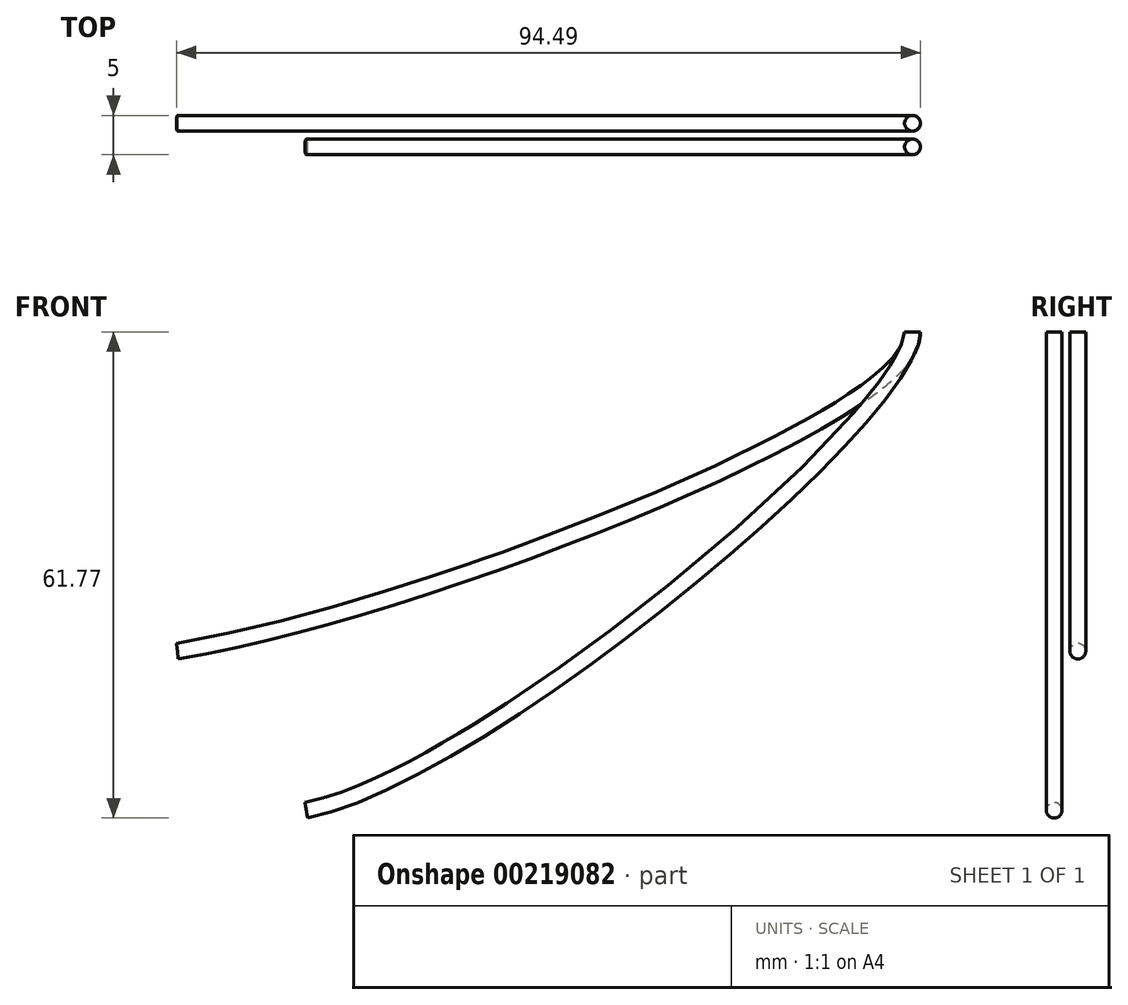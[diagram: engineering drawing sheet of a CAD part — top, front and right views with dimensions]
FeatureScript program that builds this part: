
annotation { "Feature Type Name" : "Feature", "Feature Type Description" : "" }
export const myFeature = defineFeature(function(context is Context, id is Id, definition is map)
    precondition{}
    {
        {
            var Q0;
            Q0=qCreatedBy(makeId("Front.planeOp"),FACE);
            var sketch = newSketch(context, id + "F0", { "sketchPlane" : qUnion([Q0])});
            skLineSegment(sketch, "E0", {"start": v(-1.5, 0) * mm, "end": v(1.5, 0) * mm, "construction": true});
            skFitSpline(sketch, "E1", {"points": [v(-1.5, 0) * mm, v(-93.55, -39.07) * mm], "startDerivative": vector(1.4, -27.44) * mm, "endDerivative": vector(-96.15, -16.1) * mm});
            skFitSpline(sketch, "E2", {"points": [v(1.5, 0) * mm, v(-76.76, -62.26) * mm], "startDerivative": vector(0.49, -35.49) * mm, "endDerivative": vector(-66.07, -12.31) * mm});
            skSolve(sketch);
        }
        {
            var Q0;
            Q0=qCreatedBy(makeId("Top.planeOp"),FACE);
            var sketch = newSketch(context, id + "F1", { "sketchPlane" : qUnion([Q0])});
            skCircle(sketch, "E3", {"center": v(0, 1.5) * mm, "radius": 1 * mm});
            skCircle(sketch, "E4", {"center": v(0, -1.5) * mm, "radius": 1 * mm});
            skLineSegment(sketch, "E5", {"start": v(0, -3.4) * mm, "end": v(0, 4.85) * mm, "construction": true});
            skCircle(sketch, "E6", {"center": v(0, 0) * mm, "radius": 1.5 * mm, "construction": true});
            skSolve(sketch);
        }
        {
            var Q0;
            Q0=makeQuery(id+"F1.imprint","IMPRINT",FACE,{"disambiguationData":[TD([[makeQuery(id+"F1.imprint","IMPRINT",EDGE,{"derivedFrom":sQuery(id+"F1.wireOp",EDGE,"E4")}),1.0]])]});
            var Q1;
            Q1=sQuery(id+"F1.wireOp",EDGE,"E4");
            var Q2;
            Q2=sQuery(id+"F0.wireOp",EDGE,"E2");
            sweep(context, id + "F2", {"profiles" : qUnion([Q0]), "surfaceProfiles" : qUnion([Q1]), "path" : qUnion([Q2])});
        }
        {
            var Q0;
            Q0=makeQuery(id+"F1.imprint","IMPRINT",FACE,{"disambiguationData":[TD([[makeQuery(id+"F1.imprint","IMPRINT",EDGE,{"derivedFrom":sQuery(id+"F1.wireOp",EDGE,"E3")}),1.0]])]});
            var Q1;
            Q1=sQuery(id+"F0.wireOp",EDGE,"E1");
            sweep(context, id + "F3", {"profiles" : qUnion([Q0]), "path" : qUnion([Q1])});
        }
    });
